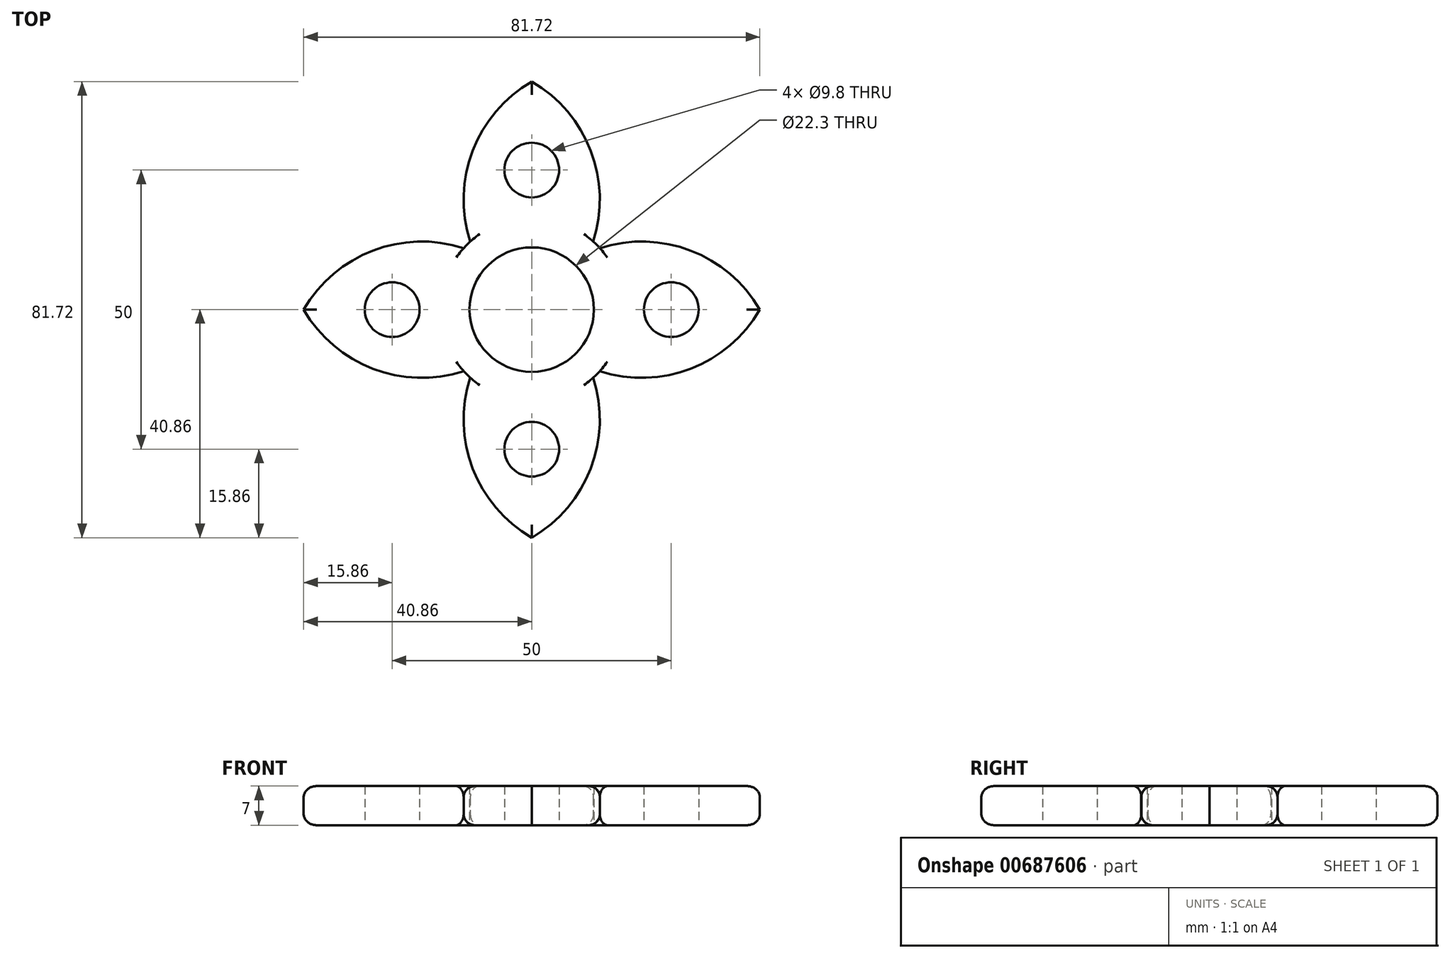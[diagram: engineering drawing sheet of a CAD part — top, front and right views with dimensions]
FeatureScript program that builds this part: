
annotation { "Feature Type Name" : "Feature", "Feature Type Description" : "" }
export const myFeature = defineFeature(function(context is Context, id is Id, definition is map)
    precondition{}
    {
        {
            var Q0;
            Q0=qCreatedBy(makeId("Top.planeOp"),FACE);
            var sketch = newSketch(context, id + "F0", { "sketchPlane" : qUnion([Q0])});
            skCircle(sketch, "E0", {"center": v(0, 0) * mm, "radius": 11.15 * mm});
            skCircle(sketch, "E1", {"center": v(25, 0) * mm, "radius": 4.9 * mm});
            skCircle(sketch, "E2", {"center": v(0, 0) * mm, "radius": 16.44 * mm});
            skCircle(sketch, "E3", {"center": v(25, 0) * mm, "radius": 7.93 * mm});
            skArc(sketch, "E4", {"start": v(40.86, 0) * mm, "mid": v(28.48, 10.57) * mm, "end": v(12.2, 11.02) * mm});
            skArc(sketch, "E5.MirrorCS", {"start": v(40.86, 0) * mm, "mid": v(28.48, -10.57) * mm, "end": v(12.2, -11.02) * mm});
            skArc(sketch, "E6.1.0", {"start": v(0, 40.86) * mm, "mid": v(-10.57, 28.48) * mm, "end": v(-11.02, 12.2) * mm});
            skArc(sketch, "E6.1.1", {"start": v(0, 40.86) * mm, "mid": v(10.57, 28.48) * mm, "end": v(11.02, 12.2) * mm});
            skCircle(sketch, "E6.1.2", {"center": v(0, 25) * mm, "radius": 4.9 * mm});
            skArc(sketch, "E6.2.0", {"start": v(-40.86, 0) * mm, "mid": v(-28.48, -10.57) * mm, "end": v(-12.2, -11.02) * mm});
            skArc(sketch, "E6.2.1", {"start": v(-40.86, 0) * mm, "mid": v(-28.48, 10.57) * mm, "end": v(-12.2, 11.02) * mm});
            skCircle(sketch, "E6.2.2", {"center": v(-25, 0) * mm, "radius": 4.9 * mm});
            skArc(sketch, "E6.3.0", {"start": v(0, -40.86) * mm, "mid": v(10.57, -28.48) * mm, "end": v(11.02, -12.2) * mm});
            skArc(sketch, "E6.3.1", {"start": v(0, -40.86) * mm, "mid": v(-10.57, -28.48) * mm, "end": v(-11.02, -12.2) * mm});
            skCircle(sketch, "E6.3.2", {"center": v(0, -25) * mm, "radius": 4.9 * mm});
            skSolve(sketch);
        }
        {
            var Q0;
            Q0=makeQuery(id+"F0.imprint","IMPRINT",FACE,{"disambiguationData":[TD([[makeQuery(id+"F0.imprint","IMPRINT",EDGE,{"derivedFrom":sQuery(id+"F0.wireOp",EDGE,"E1")}),-1.0]])]});
            var Q1;
            {var subQ0=sQuery(id+"F0.wireOp",EDGE,"E6.1.0");Q1=makeQuery(id+"F0.imprint","IMPRINT",FACE,{"disambiguationData":[TD([[makeQuery(id+"F0.imprint","IMPRINT",EDGE,{"derivedFrom":subQ0}),1.0]])]});}
            var Q2;
            {var subQ0=sQuery(id+"F0.wireOp",EDGE,"E6.3.0");Q2=makeQuery(id+"F0.imprint","IMPRINT",FACE,{"disambiguationData":[TD([[makeQuery(id+"F0.imprint","IMPRINT",EDGE,{"derivedFrom":subQ0}),1.0]])]});}
            var Q3;
            Q3=makeQuery(id+"F0.imprint","IMPRINT",FACE,{"disambiguationData":[TD([[makeQuery(id+"F0.imprint","IMPRINT",EDGE,{"derivedFrom":sQuery(id+"F0.wireOp",EDGE,"E3")}),-1.0]])]});
            var Q4;
            Q4=makeQuery(id+"F0.imprint","IMPRINT",FACE,{"disambiguationData":[TD([[makeQuery(id+"F0.imprint","IMPRINT",EDGE,{"derivedFrom":sQuery(id+"F0.wireOp",EDGE,"E0")}),-1.0]])]});
            var Q5;
            {var subQ0=sQuery(id+"F0.wireOp",EDGE,"E6.2.0");Q5=makeQuery(id+"F0.imprint","IMPRINT",FACE,{"disambiguationData":[TD([[makeQuery(id+"F0.imprint","IMPRINT",EDGE,{"derivedFrom":subQ0}),1.0]])]});}
            extrude(context, id + "F1", {"entities" : qUnion([Q0, Q1, Q2, Q3, Q4, Q5]), "depth" : 7 * mm, "offsetDistance" : 25 * mm});
        }
        {
            var Q0;
            Q0=makeQuery(id+"F1.opExtrude","CAP_EDGE",EDGE,{"disambiguationData":[OSD([sQuery(id+"F0.wireOp",EDGE,"E6.1.0")])],"isStart":false});
            var Q1;
            Q1=makeQuery(id+"F1.opExtrude","CAP_EDGE",EDGE,{"disambiguationData":[OSD([sQuery(id+"F0.wireOp",EDGE,"E6.1.1")])],"isStart":false});
            var Q2;
            Q2=makeQuery(id+"F1.opExtrude","CAP_EDGE",EDGE,{"disambiguationData":[OSD([sQuery(id+"F0.wireOp",EDGE,"E5.MirrorCS")])],"isStart":false});
            var Q3;
            Q3=makeQuery(id+"F1.opExtrude","CAP_EDGE",EDGE,{"disambiguationData":[OSD([sQuery(id+"F0.wireOp",EDGE,"E4")])],"isStart":false});
            var Q4;
            Q4=makeQuery(id+"F1.opExtrude","CAP_EDGE",EDGE,{"disambiguationData":[OSD([sQuery(id+"F0.wireOp",EDGE,"E6.3.0")])],"isStart":false});
            var Q5;
            Q5=makeQuery(id+"F1.opExtrude","CAP_EDGE",EDGE,{"disambiguationData":[OSD([sQuery(id+"F0.wireOp",EDGE,"E6.3.1")])],"isStart":false});
            var Q6;
            Q6=makeQuery(id+"F1.opExtrude","CAP_EDGE",EDGE,{"disambiguationData":[OSD([sQuery(id+"F0.wireOp",EDGE,"E6.2.0")])],"isStart":false});
            var Q7;
            Q7=makeQuery(id+"F1.opExtrude","CAP_EDGE",EDGE,{"disambiguationData":[OSD([sQuery(id+"F0.wireOp",EDGE,"E6.2.1")])],"isStart":false});
            var Q8;
            Q8=makeQuery(id+"F1.opExtrude","CAP_EDGE",EDGE,{"disambiguationData":[OSD([sQuery(id+"F0.wireOp",EDGE,"E6.1.1")])],"isStart":true});
            var Q9;
            Q9=makeQuery(id+"F1.opExtrude","CAP_EDGE",EDGE,{"disambiguationData":[OSD([sQuery(id+"F0.wireOp",EDGE,"E6.1.0")])],"isStart":true});
            var Q10;
            Q10=makeQuery(id+"F1.opExtrude","CAP_EDGE",EDGE,{"disambiguationData":[OSD([sQuery(id+"F0.wireOp",EDGE,"E6.2.1")])],"isStart":true});
            var Q11;
            Q11=makeQuery(id+"F1.opExtrude","CAP_EDGE",EDGE,{"disambiguationData":[OSD([sQuery(id+"F0.wireOp",EDGE,"E6.2.0")])],"isStart":true});
            var Q12;
            Q12=makeQuery(id+"F1.opExtrude","CAP_EDGE",EDGE,{"disambiguationData":[OSD([sQuery(id+"F0.wireOp",EDGE,"E6.3.0")])],"isStart":true});
            var Q13;
            Q13=makeQuery(id+"F1.opExtrude","CAP_EDGE",EDGE,{"disambiguationData":[OSD([sQuery(id+"F0.wireOp",EDGE,"E6.3.1")])],"isStart":true});
            var Q14;
            Q14=makeQuery(id+"F1.opExtrude","CAP_EDGE",EDGE,{"disambiguationData":[OSD([sQuery(id+"F0.wireOp",EDGE,"E4")])],"isStart":true});
            var Q15;
            Q15=makeQuery(id+"F1.opExtrude","CAP_EDGE",EDGE,{"disambiguationData":[OSD([sQuery(id+"F0.wireOp",EDGE,"E5.MirrorCS")])],"isStart":true});
            fillet(context, id + "F2", {"entities" : qUnion([Q0, Q1, Q2, Q3, Q4, Q5, Q6, Q7, Q8, Q9, Q10, Q11, Q12, Q13, Q14, Q15]), "radius" : 2 * mm, "tangentPropagation" : true, "allowEdgeOverflow" : false});
        }
    });
